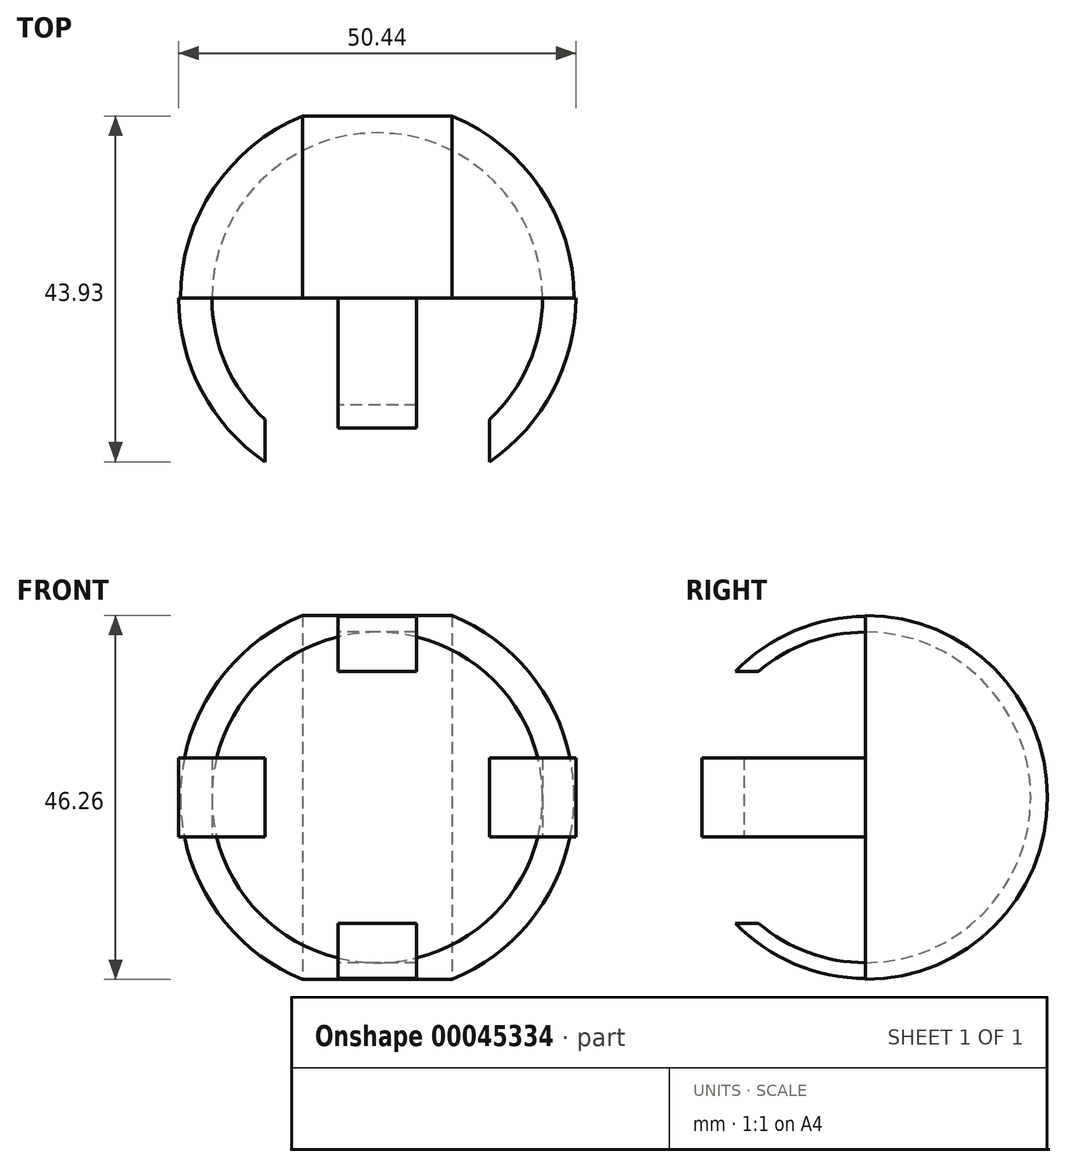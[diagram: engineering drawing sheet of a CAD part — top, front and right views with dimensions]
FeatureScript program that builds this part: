
annotation { "Feature Type Name" : "Feature", "Feature Type Description" : "" }
export const myFeature = defineFeature(function(context is Context, id is Id, definition is map)
    precondition{}
    {
        {
            var Q0;
            Q0=qCreatedBy(makeId("Top.planeOp"),FACE);
            var sketch = newSketch(context, id + "F0", { "sketchPlane" : qUnion([Q0])});
            skArc(sketch, "E0", {"start": v(21, 0) * mm, "mid": v(0, 21) * mm, "end": v(-21, 0) * mm});
            skArc(sketch, "E1", {"start": v(25, 0) * mm, "mid": v(20.77, 13.92) * mm, "end": v(9.5, 23.13) * mm});
            skLineSegment(sketch, "E2", {"start": v(-25, 0) * mm, "end": v(-21, 0) * mm});
            skLineSegment(sketch, "E3", {"start": v(-9.5, 23.13) * mm, "end": v(9.5, 23.13) * mm});
            skLineSegment(sketch, "E4.trimOffspring", {"start": v(21, 0) * mm, "end": v(25, 0) * mm});
            skArc(sketch, "E5.trimOffspring", {"start": v(-9.5, 23.13) * mm, "mid": v(-20.77, 13.92) * mm, "end": v(-25, 0) * mm});
            skSolve(sketch);
        }
        {
            var Q0;
            Q0 = qSketchRegion(id + "F0", true);
            var Q1;
            Q1=sQuery(id+"F0.wireOp",EDGE,"E4.trimOffspring");
            revolve(context, id + "F1", {"entities" : qUnion([Q0]), "axis" : qUnion([Q1]), "revolveType" : RevolveType.SYMMETRIC, "angle" : 180 * degree});
        }
        {
            var Q0;
            Q0=qCreatedBy(makeId("Top.planeOp"),FACE);
            var sketch = newSketch(context, id + "F2", { "sketchPlane" : qUnion([Q0])});
            skArc(sketch, "E6", {"start": v(14.27, -15.41) * mm, "mid": v(0, 21) * mm, "end": v(-14.27, -15.41) * mm});
            skArc(sketch, "E7", {"start": v(-25.22, 0) * mm, "mid": v(-22.32, -11.75) * mm, "end": v(-14.27, -20.8) * mm});
            skLineSegment(sketch, "E8", {"start": v(-25.22, 0) * mm, "end": v(-21, 0) * mm});
            skLineSegment(sketch, "E9", {"start": v(-14.27, -20.8) * mm, "end": v(-14.27, -15.41) * mm});
            skLineSegment(sketch, "E10.MirrorCS", {"start": v(14.27, -20.8) * mm, "end": v(14.27, -15.41) * mm});
            skArc(sketch, "E11.trimOffspring", {"start": v(14.27, -20.8) * mm, "mid": v(22.32, -11.75) * mm, "end": v(25.22, 0) * mm});
            skPoint(sketch, "E12.orphan", {"position": v(-14.27, 0) * mm});
            skPoint(sketch, "E13.orphan", {"position": v(14.27, 0) * mm});
            skLineSegment(sketch, "E14.trimOffspring", {"start": v(21, 0) * mm, "end": v(25.22, 0) * mm});
            skLineSegment(sketch, "E15.trimOffspring", {"start": v(-14.27, 0) * mm, "end": v(14.27, 0) * mm});
            skSolve(sketch);
        }
        {
            var Q0;
            Q0 = qSketchRegion(id + "F2", true);
            extrude(context, id + "F3", {"entities" : qUnion([Q0]), "operationType" : NewBodyOperationType.ADD, "endBound" : BoundingType.SYMMETRIC, "depth" : 10 * mm});
        }
        {
            var Q0;
            Q0=qCreatedBy(makeId("Right.planeOp"),FACE);
            var sketch = newSketch(context, id + "F4", { "sketchPlane" : qUnion([Q0])});
            skArc(sketch, "E16", {"start": v(0, 21) * mm, "mid": v(-7.23, 19.72) * mm, "end": v(-13.58, 16.02) * mm});
            skArc(sketch, "E17", {"start": v(0, 23) * mm, "mid": v(-8.96, 21.18) * mm, "end": v(-16.5, 16.02) * mm});
            skLineSegment(sketch, "E18", {"start": v(0, 23) * mm, "end": v(0, 21) * mm});
            skLineSegment(sketch, "E19.trimOffspring", {"start": v(0, -21) * mm, "end": v(0, -23) * mm});
            skLineSegment(sketch, "E20", {"start": v(-16.5, -16.02) * mm, "end": v(-13.58, -16.02) * mm});
            skLineSegment(sketch, "E21.MirrorCS", {"start": v(-16.5, 16.02) * mm, "end": v(-13.58, 16.02) * mm});
            skArc(sketch, "E22.trimOffspring", {"start": v(-16.5, -16.02) * mm, "mid": v(-8.96, -21.18) * mm, "end": v(0, -23) * mm});
            skArc(sketch, "E23.trimOffspring", {"start": v(-13.58, -16.02) * mm, "mid": v(-7.23, -19.72) * mm, "end": v(0, -21) * mm});
            skPoint(sketch, "E24.orphan", {"position": v(0, -16.02) * mm});
            skPoint(sketch, "E25.orphan", {"position": v(0, 16.02) * mm});
            skSolve(sketch);
        }
        {
            var Q0;
            Q0 = qSketchRegion(id + "F4", true);
            extrude(context, id + "F5", {"entities" : qUnion([Q0]), "operationType" : NewBodyOperationType.ADD, "endBound" : BoundingType.SYMMETRIC, "depth" : 10 * mm});
        }
    });
